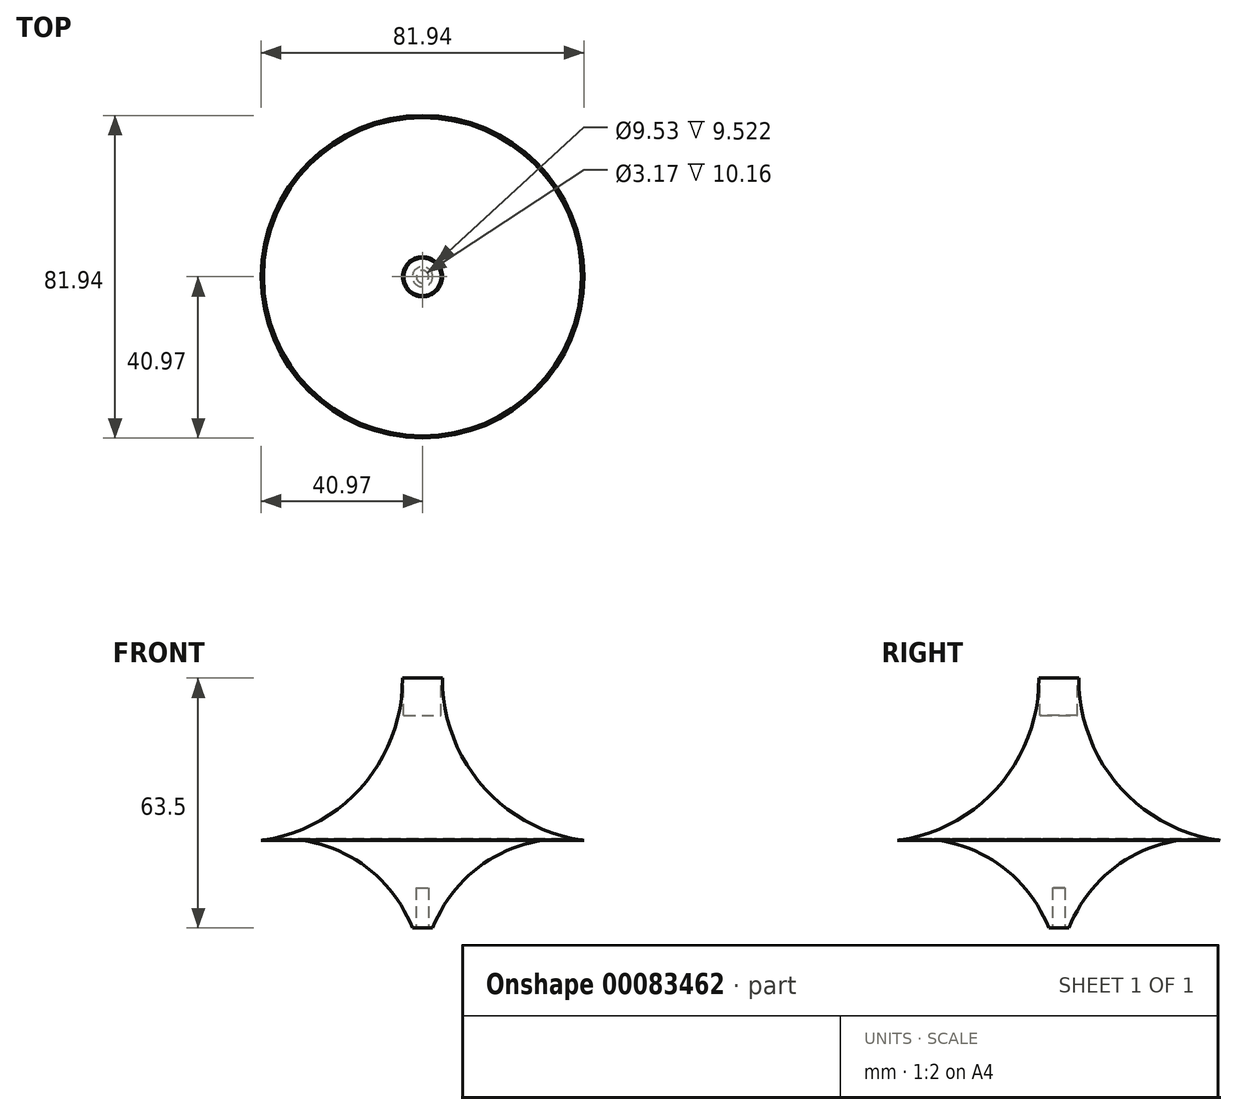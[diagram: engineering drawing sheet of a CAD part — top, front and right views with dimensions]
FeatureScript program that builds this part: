
annotation { "Feature Type Name" : "Feature", "Feature Type Description" : "" }
export const myFeature = defineFeature(function(context is Context, id is Id, definition is map)
    precondition{}
    {
        {
            var Q0;
            Q0=qCreatedBy(makeId("Front.planeOp"),FACE);
            var sketch = newSketch(context, id + "F0", { "sketchPlane" : qUnion([Q0])});
            skArc(sketch, "E0", {"start": v(5.08, 41.22) * mm, "mid": v(15.23, 13.82) * mm, "end": v(40.97, 0) * mm});
            skArc(sketch, "E1", {"start": v(40.97, 0) * mm, "mid": v(17.88, -4.44) * mm, "end": v(2.57, -22.28) * mm});
            skLineSegment(sketch, "E2", {"start": v(5.08, 41.22) * mm, "end": v(0, 41.22) * mm});
            skLineSegment(sketch, "E3", {"start": v(0, 41.22) * mm, "end": v(0, -22.28) * mm});
            skLineSegment(sketch, "E4", {"start": v(0, -22.28) * mm, "end": v(2.57, -22.28) * mm});
            skSolve(sketch);
        }
        {
            var Q0;
            Q0 = qSketchRegion(id + "F0", true);
            var Q1;
            Q1=sQuery(id+"F0.wireOp",EDGE,"E3");
            revolve(context, id + "F1", {"entities" : qUnion([Q0]), "axis" : qUnion([Q1]), "revolveType" : RevolveType.FULL});
        }
        {
            var Q0;
            Q0=qCreatedBy(makeId("Front.planeOp"),FACE);
            var sketch = newSketch(context, id + "F2", { "sketchPlane" : qUnion([Q0])});
            skLineSegment(sketch, "E5", {"start": v(0, 41.22) * mm, "end": v(4.76, 41.22) * mm});
            skLineSegment(sketch, "E6", {"start": v(4.76, 41.22) * mm, "end": v(4.76, 40.28) * mm});
            skLineSegment(sketch, "E7", {"start": v(4.76, 40.28) * mm, "end": v(0, 40.28) * mm});
            skLineSegment(sketch, "E8", {"start": v(0, 40.28) * mm, "end": v(0, 41.22) * mm});
            skSolve(sketch);
        }
        {
            var Q0;
            Q0 = qSketchRegion(id + "F2", true);
            var Q1;
            Q1=sQuery(id+"F2.wireOp",EDGE,"E8");
            revolve(context, id + "F3", {"entities" : qUnion([Q0]), "axis" : qUnion([Q1]), "revolveType" : RevolveType.FULL});
        }
        {
            var Q0;
            Q0=makeQuery(id+"F3.opRevolve","SWEPT_FACE",FACE,{"disambiguationData":[OSD([sQuery(id+"F2.wireOp",EDGE,"E5")])]});
            extrude(context, id + "F4", {"entities" : qUnion([Q0]), "operationType" : NewBodyOperationType.REMOVE, "oppositeDirection" : true, "depth" : 9.52 * mm});
        }
        {
            var Q0;
            Q0=makeQuery(id+"F1.opRevolve","SWEPT_FACE",FACE,{"disambiguationData":[OSD([sQuery(id+"F0.wireOp",EDGE,"E4")])]});
            var sketch = newSketch(context, id + "F5", { "sketchPlane" : qUnion([Q0])});
            skCircle(sketch, "E9", {"center": v(0, 0) * mm, "radius": 1.59 * mm});
            skSolve(sketch);
        }
        {
            var Q0;
            Q0=makeQuery(id+"F5.imprint","IMPRINT",FACE,{"disambiguationData":[TD([[makeQuery(id+"F5.imprint","IMPRINT",EDGE,{"derivedFrom":sQuery(id+"F5.wireOp",EDGE,"E9")}),1.0]])]});
            var Q1;
            Q1=sQuery(id+"F5.wireOp",EDGE,"E9");
            extrude(context, id + "F6", {"entities" : qUnion([Q0]), "operationType" : NewBodyOperationType.REMOVE, "surfaceEntities" : qUnion([Q1]), "oppositeDirection" : true, "depth" : 10.16 * mm});
        }
    });
